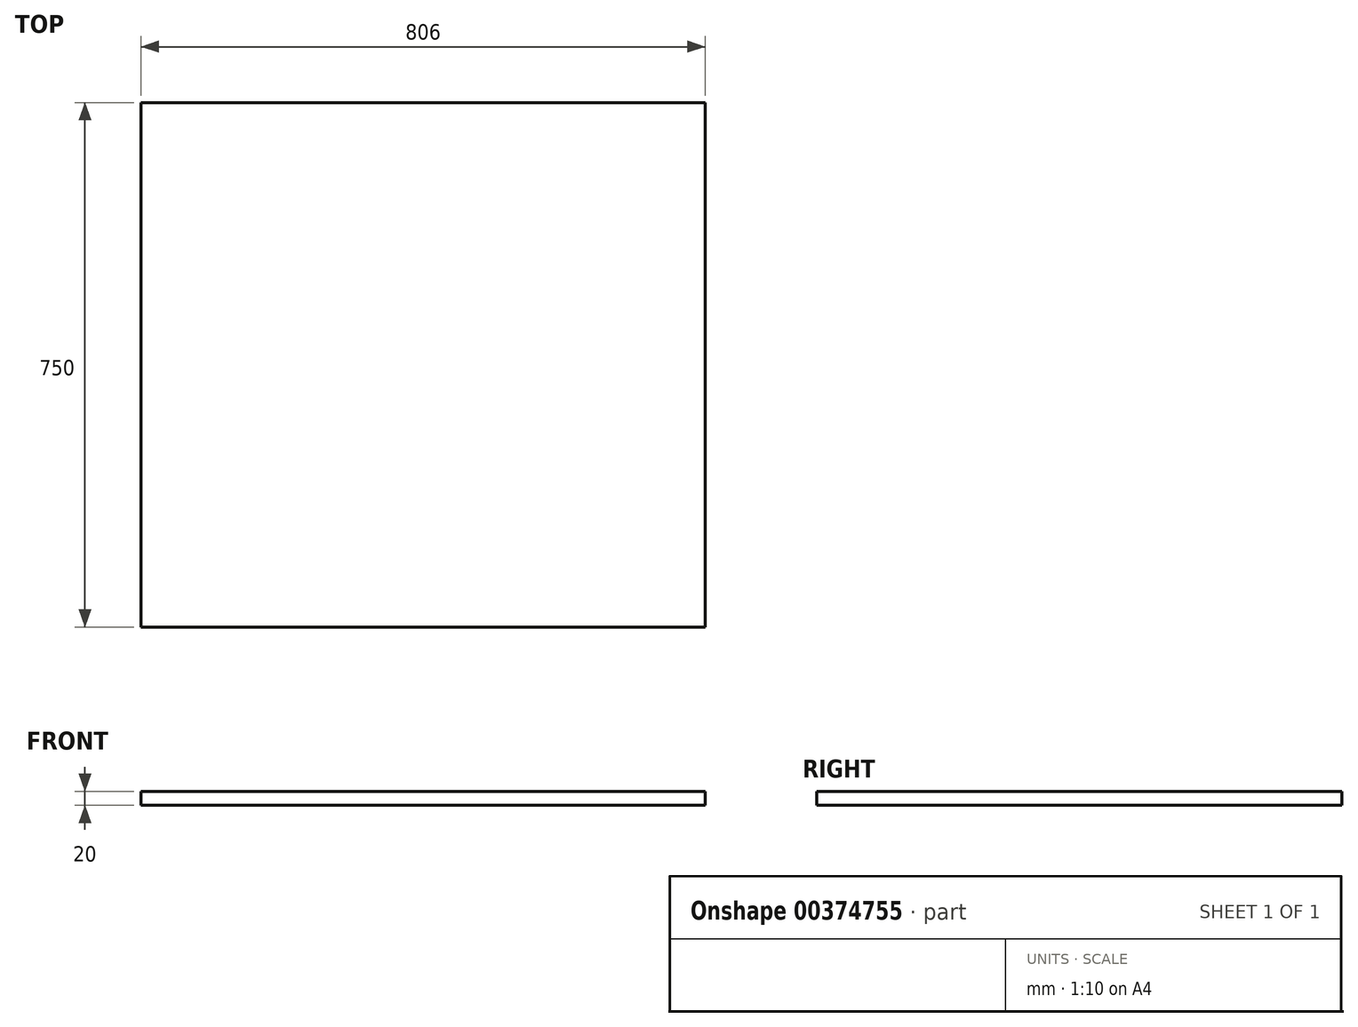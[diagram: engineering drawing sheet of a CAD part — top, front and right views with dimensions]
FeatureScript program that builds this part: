
annotation { "Feature Type Name" : "Feature", "Feature Type Description" : "" }
export const myFeature = defineFeature(function(context is Context, id is Id, definition is map)
    precondition{}
    {
        {
            var Q0;
            Q0=qCreatedBy(makeId("Top.planeOp"),FACE);
            var sketch = newSketch(context, id + "F0", { "sketchPlane" : qUnion([Q0])});
            skLineSegment(sketch, "E0.bottom", {"start": v(403, -375) * mm, "end": v(-403, -375) * mm});
            skLineSegment(sketch, "E0.top", {"start": v(403, 375) * mm, "end": v(-403, 375) * mm});
            skLineSegment(sketch, "E0.left", {"start": v(403, -375) * mm, "end": v(403, 375) * mm});
            skLineSegment(sketch, "E0.right", {"start": v(-403, -375) * mm, "end": v(-403, 375) * mm});
            skPoint(sketch, "E0.middle", {"position": v(0, 0) * mm});
            skSolve(sketch);
        }
        {
            var Q0;
            Q0=makeQuery(id+"F0.imprint","IMPRINT",FACE,{"disambiguationData":[TD([[makeQuery(id+"F0.imprint","IMPRINT",EDGE,{"derivedFrom":sQuery(id+"F0.wireOp",EDGE,"E0.bottom")}),-1.0]])]});
            extrude(context, id + "F1", {"entities" : qUnion([Q0]), "depth" : 20 * mm});
        }
    });
